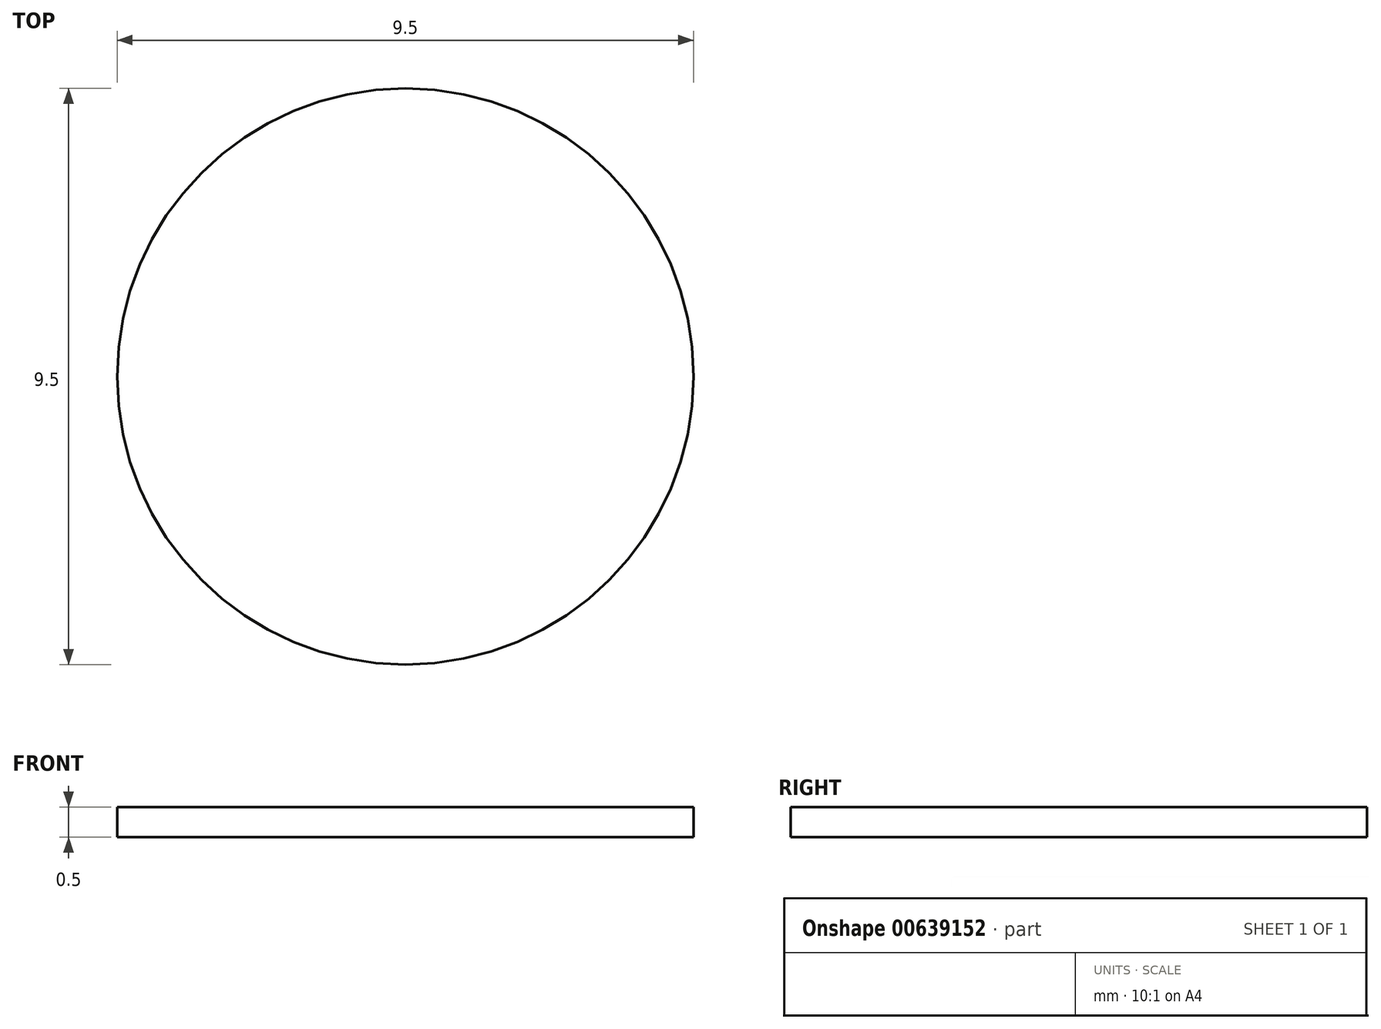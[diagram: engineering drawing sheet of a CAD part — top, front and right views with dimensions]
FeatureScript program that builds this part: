
annotation { "Feature Type Name" : "Feature", "Feature Type Description" : "" }
export const myFeature = defineFeature(function(context is Context, id is Id, definition is map)
    precondition{}
    {
        {
            var Q0;
            Q0=qCreatedBy(makeId("Top.planeOp"),FACE);
            var sketch = newSketch(context, id + "F0", { "sketchPlane" : qUnion([Q0])});
            skCircle(sketch, "E0", {"center": v(0, 0) * mm, "radius": 4.75 * mm});
            skSolve(sketch);
        }
        {
            var Q0;
            Q0 = qSketchRegion(id + "F0", true);
            extrude(context, id + "F1", {"entities" : qUnion([Q0]), "depth" : (0.25 * 2) * mm, "offsetDistance" : 25 * mm});
        }
    });
